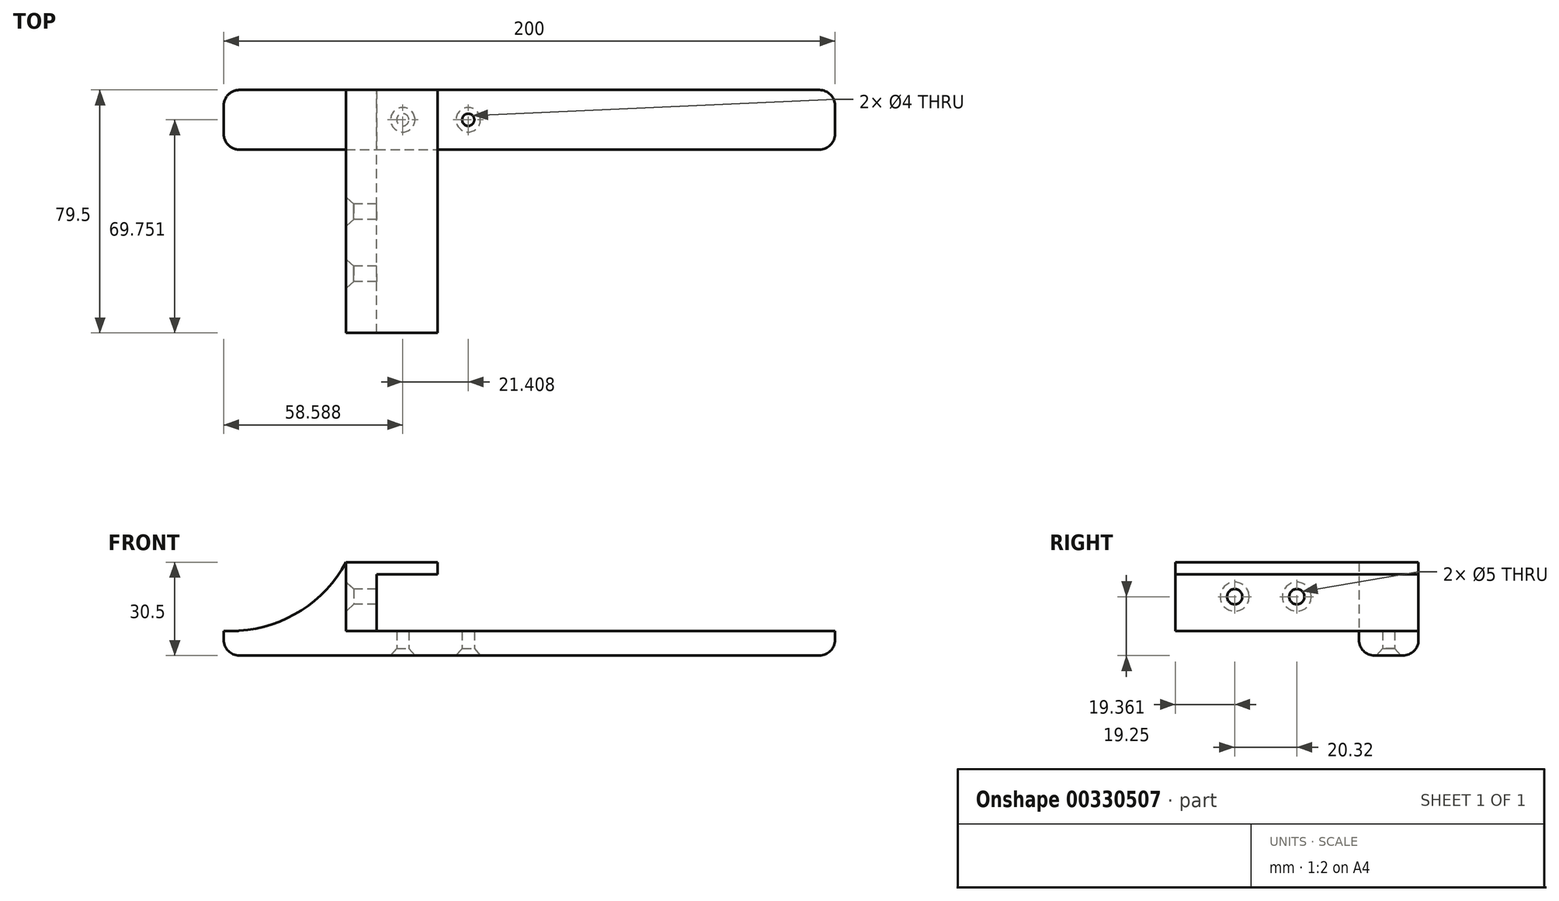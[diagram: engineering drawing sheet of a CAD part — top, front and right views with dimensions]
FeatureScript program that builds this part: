
annotation { "Feature Type Name" : "Feature", "Feature Type Description" : "" }
export const myFeature = defineFeature(function(context is Context, id is Id, definition is map)
    precondition{}
    {
        {
            var Q0;
            Q0=qCreatedBy(makeId("Top.planeOp"),FACE);
            var sketch = newSketch(context, id + "F0", { "sketchPlane" : qUnion([Q0])});
            skLineSegment(sketch, "E0.bottom", {"start": v(-23.2, 14.93) * mm, "end": v(176.8, 14.93) * mm});
            skLineSegment(sketch, "E0.top", {"start": v(-23.2, -4.57) * mm, "end": v(176.8, -4.57) * mm});
            skLineSegment(sketch, "E0.left", {"start": v(-23.2, 14.93) * mm, "end": v(-23.2, -4.57) * mm});
            skLineSegment(sketch, "E0.right", {"start": v(176.8, 14.93) * mm, "end": v(176.8, -4.57) * mm});
            skSolve(sketch);
        }
        {
            var Q0;
            Q0=makeQuery(id+"F0.imprint","IMPRINT",FACE,{"disambiguationData":[TD([[makeQuery(id+"F0.imprint","IMPRINT",EDGE,{"derivedFrom":sQuery(id+"F0.wireOp",EDGE,"E0.bottom")}),-1.0]])]});
            extrude(context, id + "F1", {"entities" : qUnion([Q0]), "depth" : 8 * mm});
        }
        {
            var Q0;
            Q0=makeQuery(id+"F1.opExtrude","CAP_FACE",FACE,{"disambiguationData":[OSD([sQuery(id+"F0.wireOp",EDGE,"E0.bottom"),sQuery(id+"F0.wireOp",EDGE,"E0.top"),sQuery(id+"F0.wireOp",EDGE,"E0.left"),sQuery(id+"F0.wireOp",EDGE,"E0.right")])],"isStart":false});
            var sketch = newSketch(context, id + "F2", { "sketchPlane" : qUnion([Q0])});
            skLineSegment(sketch, "E1", {"start": v(-23.2, -4.57) * mm, "end": v(16.8, -4.57) * mm});
            skLineSegment(sketch, "E2", {"start": v(16.8, -4.57) * mm, "end": v(16.8, 14.93) * mm});
            skLineSegment(sketch, "E3", {"start": v(16.8, 14.93) * mm, "end": v(26.8, 14.93) * mm});
            skLineSegment(sketch, "E4", {"start": v(26.8, 14.93) * mm, "end": v(26.8, -4.57) * mm});
            skLineSegment(sketch, "E5", {"start": v(26.8, -4.57) * mm, "end": v(16.8, -4.57) * mm});
            skSolve(sketch);
        }
        {
            var Q0;
            Q0=makeQuery(id+"F2.imprint","IMPRINT",FACE,{"disambiguationData":[TD([[makeQuery(id+"F2.imprint","IMPRINT",EDGE,{"derivedFrom":sQuery(id+"F2.wireOp",EDGE,"E2")}),-1.0]])]});
            extrude(context, id + "F3", {"entities" : qUnion([Q0]), "operationType" : NewBodyOperationType.ADD, "depth" : 22.5 * mm});
        }
        {
            var Q0;
            Q0=makeQuery(id+"F3.opExtrude","SWEPT_FACE",FACE,{"disambiguationData":[OSD([sQuery(id+"F2.wireOp",EDGE,"E4")])]});
            var sketch = newSketch(context, id + "F4", { "sketchPlane" : qUnion([Q0])});
            skLineSegment(sketch, "E6", {"start": v(-4.57, 8) * mm, "end": v(-4.57, 26.5) * mm});
            skLineSegment(sketch, "E7", {"start": v(-4.57, 26.5) * mm, "end": v(14.93, 26.5) * mm});
            skLineSegment(sketch, "E8", {"start": v(14.93, 26.5) * mm, "end": v(14.93, 30.5) * mm});
            skLineSegment(sketch, "E9", {"start": v(14.93, 30.5) * mm, "end": v(-4.57, 30.5) * mm});
            skLineSegment(sketch, "E10", {"start": v(-4.57, 30.5) * mm, "end": v(-4.57, 26.5) * mm});
            skSolve(sketch);
        }
        {
            var Q0;
            Q0=makeQuery(id+"F4.imprint","IMPRINT",FACE,{"disambiguationData":[TD([[makeQuery(id+"F4.imprint","IMPRINT",EDGE,{"derivedFrom":sQuery(id+"F4.wireOp",EDGE,"E7")}),1.0]])]});
            extrude(context, id + "F5", {"entities" : qUnion([Q0]), "operationType" : NewBodyOperationType.ADD, "depth" : 20 * mm});
        }
        {
            var Q0;
            Q0=makeQuery(id+"F5.boolean.opBoolean","MERGE",FACE,{"derivedFrom":[makeQuery(id+"F3.boolean.opBoolean","MERGE",FACE,{"derivedFrom":[makeQuery(id+"F1.opExtrude","SWEPT_FACE",FACE,{"disambiguationData":[OSD([sQuery(id+"F0.wireOp",EDGE,"E0.top")])]}),makeQuery(id+"F3.opExtrude","SWEPT_FACE",FACE,{"disambiguationData":[OSD([sQuery(id+"F2.wireOp",EDGE,"E5")])]})]}),makeQuery(id+"F5.opExtrude","SWEPT_FACE",FACE,{"disambiguationData":[OSD([sQuery(id+"F4.wireOp",EDGE,"E10")])]})]});
            var sketch = newSketch(context, id + "F6", { "sketchPlane" : qUnion([Q0])});
            skLineSegment(sketch, "E11", {"start": v(16.8, 8) * mm, "end": v(26.8, 8) * mm});
            skSolve(sketch);
        }
        {
            var Q0;
            Q0=makeQuery(id+"F6.imprint","IMPRINT",FACE,{"disambiguationData":[TD([[makeQuery(id+"F6.imprint","IMPRINT",EDGE,{"derivedFrom":sQuery(id+"F6.wireOp",EDGE,"E11")}),1.0]])]});
            extrude(context, id + "F7", {"entities" : qUnion([Q0]), "operationType" : NewBodyOperationType.ADD, "depth" : 60 * mm});
        }
        {
            var Q0;
            Q0=makeQuery(id+"F1.opExtrude","CAP_FACE",FACE,{"disambiguationData":[OSD([sQuery(id+"F0.wireOp",EDGE,"E0.bottom"),sQuery(id+"F0.wireOp",EDGE,"E0.top"),sQuery(id+"F0.wireOp",EDGE,"E0.left"),sQuery(id+"F0.wireOp",EDGE,"E0.right")])],"isStart":true});
            var sketch = newSketch(context, id + "F8", { "sketchPlane" : qUnion([Q0])});
            skLineSegment(sketch, "E12", {"start": v(-23.2, 4.57) * mm, "end": v(-23.2, -5.18) * mm});
            skLineSegment(sketch, "E13", {"start": v(-23.2, -5.18) * mm, "end": v(56.8, -5.18) * mm});
            skLineSegment(sketch, "E14", {"start": v(56.8, -5.18) * mm, "end": v(35.4, -5.18) * mm});
            skSolve(sketch);
        }
        {
            var Q0;
            Q0=sQuery(id+"F8.wireOp",VERTEX,"E14.end");
            var Q1;
            Q1=sQuery(id+"F8.wireOp",VERTEX,"E13.end");
            var Q2;
            Q2=makeQuery(id+"F1.opExtrude","SWEPT_BODY",BODY,{"disambiguationData":[OSD([sQuery(id+"F0.wireOp",EDGE,"E0.bottom"),sQuery(id+"F0.wireOp",EDGE,"E0.top"),sQuery(id+"F0.wireOp",EDGE,"E0.left"),sQuery(id+"F0.wireOp",EDGE,"E0.right")])]});
            hole(context, id + "F9", {"style" : HoleStyle.C_SINK, "endStyle" : HoleEndStyle.BLIND, "holeDiameter" : 4 * mm, "cSinkDiameter" : 8 * mm, "cSinkAngle" : 82 * degree, "holeDepth" : 8 * mm, "tappedDepth" : 12.7 * mm, "tapClearance" : 3, "locations" : qUnion([Q0, Q1]), "scope" : qUnion([Q2])});
        }
        {
            var Q0;
            Q0=makeQuery(id+"F3.opExtrude","CAP_EDGE",EDGE,{"disambiguationData":[OSD([sQuery(id+"F2.wireOp",EDGE,"E2")])],"isStart":true});
            fillet(context, id + "F10", {"entities" : qUnion([Q0]), "radius" : 42.92 * mm, "tangentPropagation" : true, "allowEdgeOverflow" : false});
        }
        {
            var Q0;
            {var subQ0=sQuery(id+"F2.wireOp",EDGE,"E2");Q0=makeQuery(id+"F7.boolean.opBoolean","MERGE",FACE,{"derivedFrom":[makeQuery(id+"F3.opExtrude","SWEPT_FACE",FACE,{"disambiguationData":[OSD([subQ0])]}),makeQuery(id+"F7.opExtrude","SWEPT_FACE",FACE,{"disambiguationData":[OSD([sQuery(id+"F2.wireOp",EDGE,"E1"),subQ0,sQuery(id+"F2.wireOp",EDGE,"E5")])]})]});}
            var sketch = newSketch(context, id + "F11", { "sketchPlane" : qUnion([Q0])});
            skLineSegment(sketch, "E15", {"start": v(64.57, 8) * mm, "end": v(64.57, 19.25) * mm});
            skLineSegment(sketch, "E16", {"start": v(64.57, 19.25) * mm, "end": v(4.57, 19.25) * mm});
            skLineSegment(sketch, "E17", {"start": v(4.57, 19.25) * mm, "end": v(24.89, 19.25) * mm});
            skLineSegment(sketch, "E18", {"start": v(24.89, 19.25) * mm, "end": v(45.2, 19.25) * mm});
            skSolve(sketch);
        }
        {
            var Q0;
            Q0=sQuery(id+"F11.wireOp",VERTEX,"E18.start");
            var Q1;
            Q1=sQuery(id+"F11.wireOp",VERTEX,"E18.end");
            var Q2;
            Q2=makeQuery(id+"F1.opExtrude","SWEPT_BODY",BODY,{"disambiguationData":[OSD([sQuery(id+"F0.wireOp",EDGE,"E0.bottom"),sQuery(id+"F0.wireOp",EDGE,"E0.top"),sQuery(id+"F0.wireOp",EDGE,"E0.left"),sQuery(id+"F0.wireOp",EDGE,"E0.right")])]});
            hole(context, id + "F12", {"style" : HoleStyle.C_SINK, "endStyle" : HoleEndStyle.BLIND, "holeDiameter" : 5 * mm, "cSinkDiameter" : 9.5 * mm, "cSinkAngle" : 82 * degree, "holeDepth" : 20 * mm, "tappedDepth" : 12.7 * mm, "tapClearance" : 3, "locations" : qUnion([Q0, Q1]), "scope" : qUnion([Q2])});
        }
        {
            var Q0;
            Q0=makeQuery(id+"F1.opExtrude","CAP_EDGE",EDGE,{"disambiguationData":[OSD([sQuery(id+"F0.wireOp",EDGE,"E0.top")])],"isStart":true});
            var Q1;
            Q1=makeQuery(id+"F1.opExtrude","CAP_EDGE",EDGE,{"disambiguationData":[OSD([sQuery(id+"F0.wireOp",EDGE,"E0.right")])],"isStart":true});
            var Q2;
            Q2=makeQuery(id+"F1.opExtrude","CAP_EDGE",EDGE,{"disambiguationData":[OSD([sQuery(id+"F0.wireOp",EDGE,"E0.bottom")])],"isStart":true});
            var Q3;
            Q3=makeQuery(id+"F1.opExtrude","CAP_EDGE",EDGE,{"disambiguationData":[OSD([sQuery(id+"F0.wireOp",EDGE,"E0.left")])],"isStart":true});
            var Q4;
            Q4=makeQuery(id+"F1.opExtrude","SWEPT_EDGE",EDGE,{"disambiguationData":[OSD([sQuery(id+"F0.wireOp",EDGE,"E0.bottom"),sQuery(id+"F0.wireOp",EDGE,"E0.right")])]});
            var Q5;
            Q5=makeQuery(id+"F1.opExtrude","SWEPT_EDGE",EDGE,{"disambiguationData":[OSD([sQuery(id+"F0.wireOp",EDGE,"E0.top"),sQuery(id+"F0.wireOp",EDGE,"E0.right")])]});
            var Q6;
            Q6=makeQuery(id+"F1.opExtrude","SWEPT_EDGE",EDGE,{"disambiguationData":[OSD([sQuery(id+"F0.wireOp",EDGE,"E0.bottom"),sQuery(id+"F0.wireOp",EDGE,"E0.left")])]});
            var Q7;
            Q7=makeQuery(id+"F1.opExtrude","SWEPT_EDGE",EDGE,{"disambiguationData":[OSD([sQuery(id+"F0.wireOp",EDGE,"E0.top"),sQuery(id+"F0.wireOp",EDGE,"E0.left")])]});
            fillet(context, id + "F13", {"entities" : qUnion([Q0, Q1, Q2, Q3, Q4, Q5, Q6, Q7]), "radius" : 5.08 * mm, "tangentPropagation" : true, "allowEdgeOverflow" : false});
        }
    });
